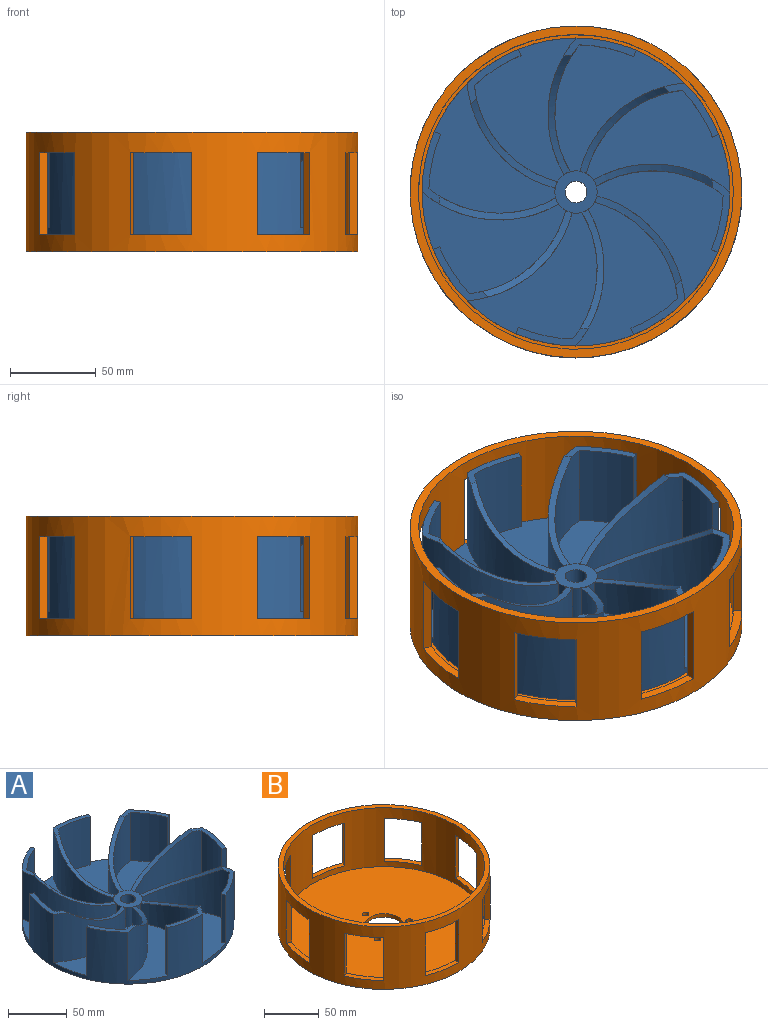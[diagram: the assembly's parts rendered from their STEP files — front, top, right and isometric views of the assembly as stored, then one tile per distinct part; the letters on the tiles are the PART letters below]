
ASSEMBLY  parts=2 mates=1
PART A: 61 faces, bbox 180x180x54 mm
  f0: plane 84.06x59.47mm, normal (0,0,1), area 2654.8mm2, adj f16,f26,f27,f29,f30,f59
  f1: plane 76.02x74.12mm, normal (0,0,1), area 2654.8mm2, adj f16,f19,f21,f22,f28,f59
  f2: plane 84.06x59.47mm, normal (0,0,1), area 2654.8mm2, adj f16,f20,f31,f32,f33,f59
  f3: plane 76.02x74.12mm, normal (0,0,1), area 2654.8mm2, adj f16,f34,f35,f36,f37,f59
  f4: plane 84.06x59.47mm, normal (0,0,1), area 2654.8mm2, adj f16,f38,f39,f40,f41,f59
  f5: plane 76.02x74.12mm, normal (0,0,1), area 2654.8mm2, adj f16,f42,f43,f44,f45,f59
  f6: plane 84.06x59.47mm, normal (0,0,1), area 2654.8mm2, adj f16,f46,f47,f48,f49,f59
  f7: plane 42.46x10.88mm, normal (0,0,1), area 177.8mm2, adj f16,f19,f20,f21,f22,f58
  f8: plane 42.46x10.88mm, normal (0,0,1), area 177.8mm2, adj f16,f23,f24,f25,f26,f57
  f9: plane 32.23x31.53mm, normal (0,0,1), area 177.8mm2, adj f16,f27,f28,f29,f30,f56
  f10: plane 32.23x31.53mm, normal (0,0,1), area 177.8mm2, adj f16,f31,f32,f33,f34,f55
  f11: plane 42.46x10.88mm, normal (0,0,1), area 177.8mm2, adj f16,f35,f36,f37,f38,f54
  f12: plane 32.23x31.53mm, normal (0,0,1), area 177.8mm2, adj f16,f39,f40,f41,f42,f53
  f13: plane 42.46x10.88mm, normal (0,0,1), area 177.8mm2, adj f16,f43,f44,f45,f46,f52
  f14: plane 32.23x31.53mm, normal (0,0,1), area 177.8mm2, adj f16,f47,f48,f49,f50,f51
  f15: plane 76.02x74.12mm, normal (0,0,1), area 2654.8mm2, adj f16,f23,f24,f25,f50,f59
  f16: cylinder r=90mm len=180mm, axis (0,0,1), area 16759.7mm2, adj f0,f1,f2,f3,f4,f5,f6,f7
  f17: cylinder r=6.35mm len=25mm, axis (0,0,1), area 997.5mm2, adj f18,f60
  f18: plane 180x180mm, normal (0,0,-1), area 25320.2mm2, adj f16,f17
  f19: plane 50x3.68mm, normal (0.92,-0.39,0), area 200mm2, adj f1,f7,f16,f22
  f20: cylinder r=70mm len=79.88mm, axis (0,0,-1), area 2931mm2, adj f2,f7,f16,f58,f59
  f21: cylinder r=66mm len=74.12mm, axis (0,0,-1), area 2629.3mm2, adj f1,f7,f22,f58,f59
  f22: cylinder r=86mm len=50mm, axis (0,0,-1), area 1637.6mm2, adj f1,f7,f19,f21
  f23: cylinder r=66mm len=74.12mm, axis (0,0,-1), area 2629.3mm2, adj f8,f15,f24,f57,f59
  f24: cylinder r=86mm len=50mm, axis (0,0,-1), area 1637.6mm2, adj f8,f15,f23,f25
  f25: plane 50x3.68mm, normal (-0.39,-0.92,0), area 200mm2, adj f8,f15,f16,f24
  f26: cylinder r=70mm len=79.88mm, axis (0,0,-1), area 2931mm2, adj f0,f8,f16,f57,f59
  f27: plane 50x3.71mm, normal (0.37,-0.93,0), area 200mm2, adj f0,f9,f16,f30
  f28: cylinder r=70mm len=61.48mm, axis (0,0,-1), area 2931mm2, adj f1,f9,f16,f56,f59
  f29: cylinder r=66mm len=56.19mm, axis (0,0,-1), area 2629.3mm2, adj f0,f9,f30,f56,f59
  f30: cylinder r=86mm len=50mm, axis (0,0,-1), area 1637.6mm2, adj f0,f9,f27,f29
  f31: cylinder r=66mm len=56.19mm, axis (0,0,-1), area 2629.3mm2, adj f2,f10,f32,f55,f59
  f32: cylinder r=86mm len=50mm, axis (0,0,-1), area 1637.6mm2, adj f2,f10,f31,f33
  f33: plane 50x3.71mm, normal (0.93,0.37,0), area 200mm2, adj f2,f10,f16,f32
  f34: cylinder r=70mm len=61.48mm, axis (0,0,-1), area 2931mm2, adj f3,f10,f16,f55,f59
  f35: cylinder r=66mm len=74.12mm, axis (0,0,-1), area 2629.3mm2, adj f3,f11,f36,f54,f59
  f36: cylinder r=86mm len=50mm, axis (0,0,-1), area 1637.6mm2, adj f3,f11,f35,f37
  f37: plane 50x3.68mm, normal (0.39,0.92,0), area 200mm2, adj f3,f11,f16,f36
  f38: cylinder r=70mm len=79.88mm, axis (0,0,-1), area 2931mm2, adj f4,f11,f16,f54,f59
  f39: cylinder r=66mm len=56.19mm, axis (0,0,-1), area 2629.3mm2, adj f4,f12,f40,f53,f59
  f40: cylinder r=86mm len=50mm, axis (0,0,-1), area 1637.6mm2, adj f4,f12,f39,f41
  f41: plane 50x3.71mm, normal (-0.37,0.93,0), area 200mm2, adj f4,f12,f16,f40
  f42: cylinder r=70mm len=61.48mm, axis (0,0,-1), area 2931mm2, adj f5,f12,f16,f53,f59
  f43: cylinder r=66mm len=74.12mm, axis (0,0,-1), area 2629.3mm2, adj f5,f13,f44,f52,f59
  f44: cylinder r=86mm len=50mm, axis (0,0,-1), area 1637.6mm2, adj f5,f13,f43,f45
  f45: plane 50x3.68mm, normal (-0.92,0.39,0), area 200mm2, adj f5,f13,f16,f44
  f46: cylinder r=70mm len=79.88mm, axis (0,0,-1), area 2931mm2, adj f6,f13,f16,f52,f59
  f47: cylinder r=66mm len=56.19mm, axis (0,0,-1), area 2629.3mm2, adj f6,f14,f48,f51,f59
  f48: cylinder r=86mm len=50mm, axis (0,0,-1), area 1637.6mm2, adj f6,f14,f47,f49
  f49: plane 50x3.71mm, normal (-0.93,-0.37,0), area 200mm2, adj f6,f14,f16,f48
  f50: cylinder r=70mm len=61.48mm, axis (0,0,-1), area 2931mm2, adj f14,f15,f16,f51,f59
  f51: sphere r=121.67mm, area 320.9mm2, adj f14,f47,f50,f59
  f52: sphere r=121.67mm, area 320.9mm2, adj f13,f43,f46,f59
  f53: sphere r=121.67mm, area 320.9mm2, adj f12,f39,f42,f59
  f54: sphere r=121.67mm, area 320.9mm2, adj f11,f35,f38,f59
  f55: sphere r=121.67mm, area 320.9mm2, adj f10,f31,f34,f59
  f56: sphere r=121.67mm, area 320.9mm2, adj f9,f28,f29,f59
  f57: sphere r=121.67mm, area 320.9mm2, adj f8,f23,f26,f59
  f58: sphere r=121.67mm, area 320.9mm2, adj f7,f20,f21,f59
  f59: cylinder r=12.35mm len=24.7mm, axis (0,0,-1), area 964.5mm2, adj f0,f1,f2,f3,f4,f5,f6,f15
  f60: plane 24.7x24.7mm, normal (0,0,1), area 352.5mm2, adj f17,f59
PART B: 41 faces, bbox 194x194x70 mm
  f0: cylinder r=97mm len=194mm, axis (0,0,1), area 28405.5mm2, adj f5,f7,f9,f10,f11,f12,f13,f14
  f1: cylinder r=3mm len=6mm, axis (0,0,1), area 75.4mm2, adj f5,f8
  f2: cylinder r=3mm len=6mm, axis (0,0,1), area 75.4mm2, adj f5,f8
  f3: cylinder r=3mm len=6mm, axis (0,0,1), area 75.4mm2, adj f5,f8
  f4: cylinder r=17.5mm len=35mm, axis (0,0,1), area 439.8mm2, adj f5,f8
  f5: plane 194x194mm, normal (0,0,-1), area 28512.3mm2, adj f0,f1,f2,f3,f4
  f6: cylinder r=92mm len=184mm, axis (0,0,-1), area 24629.1mm2, adj f7,f8,f9,f10,f11,f12,f13,f14
  f7: plane 194x194mm, normal (0,0,1), area 2968.8mm2, adj f0,f6
  f8: plane 184x184mm, normal (0,0,1), area 25543.5mm2, adj f1,f2,f3,f4,f6
  f9: plane 48x5mm, normal (1,0,0), area 240mm2, adj f0,f6,f11,f12
  f10: plane 48x4.64mm, normal (-0.93,0.37,0), area 240mm2, adj f0,f6,f11,f12
  f11: plane 36.23x11.66mm, normal (0,0,-1), area 180.9mm2, adj f0,f6,f9,f10
  f12: plane 36.23x11.66mm, normal (0,0,1), area 180.9mm2, adj f0,f6,f9,f10
  f13: plane 48x3.54mm, normal (0.71,0.71,0), area 240mm2, adj f0,f6,f15,f16
  f14: plane 48x4.6mm, normal (-0.92,-0.39,0), area 240mm2, adj f0,f6,f15,f16
  f15: plane 32.54x24.19mm, normal (0,0,-1), area 180.9mm2, adj f0,f6,f13,f14
  f16: plane 32.54x24.19mm, normal (0,0,1), area 180.9mm2, adj f0,f6,f13,f14
  f17: plane 48x5mm, normal (0,1,0), area 240mm2, adj f0,f6,f19,f20
  f18: plane 48x4.64mm, normal (-0.37,-0.93,0), area 240mm2, adj f0,f6,f19,f20
  f19: plane 36.23x11.66mm, normal (0,0,-1), area 180.9mm2, adj f0,f6,f17,f18
  f20: plane 36.23x11.66mm, normal (0,0,1), area 180.9mm2, adj f0,f6,f17,f18
  f21: plane 48x3.54mm, normal (-0.71,0.71,0), area 240mm2, adj f0,f6,f23,f24
  f22: plane 48x4.6mm, normal (0.39,-0.92,0), area 240mm2, adj f0,f6,f23,f24
  f23: plane 32.54x24.19mm, normal (0,0,-1), area 180.9mm2, adj f0,f6,f21,f22
  f24: plane 32.54x24.19mm, normal (0,0,1), area 180.9mm2, adj f0,f6,f21,f22
  f25: plane 48x5mm, normal (-1,0,0), area 240mm2, adj f0,f6,f27,f28
  f26: plane 48x4.64mm, normal (0.93,-0.37,0), area 240mm2, adj f0,f6,f27,f28
  f27: plane 36.23x11.66mm, normal (0,0,-1), area 180.9mm2, adj f0,f6,f25,f26
  f28: plane 36.23x11.66mm, normal (0,0,1), area 180.9mm2, adj f0,f6,f25,f26
  f29: plane 48x4.6mm, normal (0.92,0.39,0), area 240mm2, adj f0,f6,f31,f32
  f30: plane 48x3.54mm, normal (-0.71,-0.71,0), area 240mm2, adj f0,f6,f31,f32
  f31: plane 32.54x24.19mm, normal (0,0,-1), area 180.9mm2, adj f0,f6,f29,f30
  f32: plane 32.54x24.19mm, normal (0,0,1), area 180.9mm2, adj f0,f6,f29,f30
  f33: plane 48x4.64mm, normal (0.37,0.93,0), area 240mm2, adj f0,f6,f35,f36
  f34: plane 48x5mm, normal (0,-1,0), area 240mm2, adj f0,f6,f35,f36
  f35: plane 36.23x11.66mm, normal (0,0,-1), area 180.9mm2, adj f0,f6,f33,f34
  f36: plane 36.23x11.66mm, normal (0,0,1), area 180.9mm2, adj f0,f6,f33,f34
  f37: plane 48x3.54mm, normal (0.71,-0.71,0), area 240mm2, adj f0,f6,f39,f40
  f38: plane 48x4.6mm, normal (-0.39,0.92,0), area 240mm2, adj f0,f6,f39,f40
  f39: plane 32.54x24.19mm, normal (0,0,-1), area 180.9mm2, adj f0,f6,f37,f38
  f40: plane 32.54x24.19mm, normal (0,0,1), area 180.9mm2, adj f0,f6,f37,f38
PLACE A t=(0,0,14)mm
PLACE B t=(0,0,10)mm
MATE fastened B.f4 <-> A.f16  axis (0,0,1) through (0,0,10)mm
